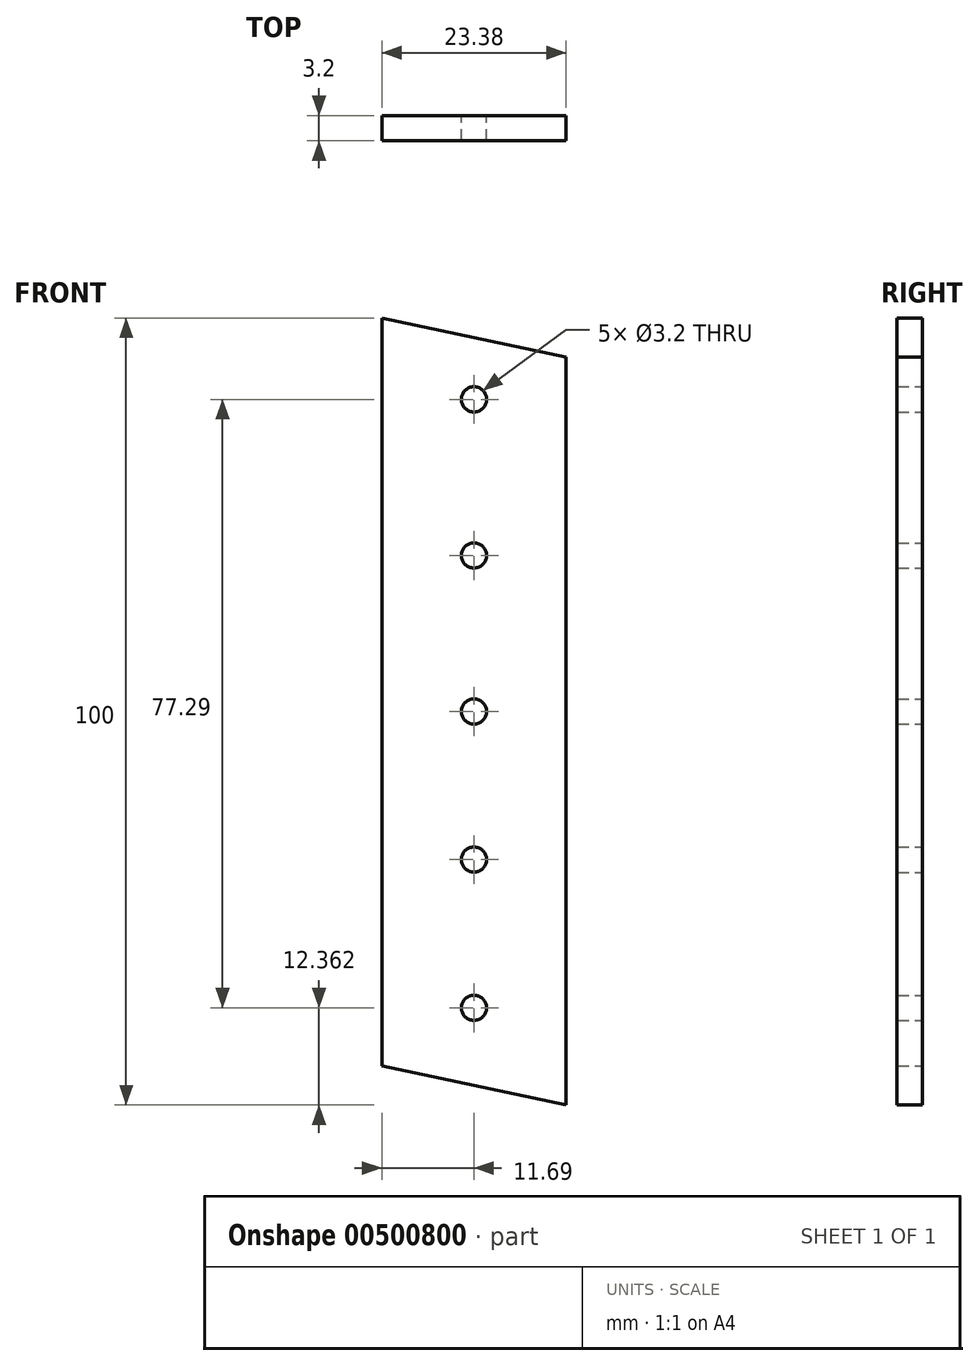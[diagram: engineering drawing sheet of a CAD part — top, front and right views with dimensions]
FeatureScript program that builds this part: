
annotation { "Feature Type Name" : "Feature", "Feature Type Description" : "" }
export const myFeature = defineFeature(function(context is Context, id is Id, definition is map)
    precondition{}
    {
        {
            var Q0;
            Q0=qCreatedBy(makeId("Front.planeOp"),FACE);
            var sketch = newSketch(context, id + "F0", { "sketchPlane" : qUnion([Q0])});
            skLineSegment(sketch, "E0.bottom", {"start": v(11.69, 45) * mm, "end": v(-11.69, 45) * mm});
            skLineSegment(sketch, "E0.top", {"start": v(11.69, -45) * mm, "end": v(-11.69, -45) * mm});
            skLineSegment(sketch, "E0.left", {"start": v(11.69, 45) * mm, "end": v(11.69, -45) * mm});
            skLineSegment(sketch, "E0.right", {"start": v(-11.69, 45) * mm, "end": v(-11.69, -45) * mm});
            skPoint(sketch, "E0.middle", {"position": v(0, 0) * mm});
            skLineSegment(sketch, "E1", {"start": v(-11.69, 45) * mm, "end": v(-11.69, 50) * mm});
            skLineSegment(sketch, "E2", {"start": v(11.69, -45) * mm, "end": v(11.69, -50) * mm});
            skLineSegment(sketch, "E3", {"start": v(-11.69, -45) * mm, "end": v(11.69, -50) * mm});
            skLineSegment(sketch, "E4", {"start": v(-11.69, 50) * mm, "end": v(11.69, 45) * mm});
            skPoint(sketch, "E5", {"position": v(0, -37.64) * mm});
            skPoint(sketch, "E6", {"position": v(0, 39.65) * mm});
            skCircle(sketch, "E7", {"center": v(0, 39.65) * mm, "radius": 1.6 * mm});
            skCircle(sketch, "E8", {"center": v(0, 0) * mm, "radius": 1.6 * mm});
            skCircle(sketch, "E9", {"center": v(0, -37.64) * mm, "radius": 1.6 * mm});
            skLineSegment(sketch, "E10", {"start": v(0, 39.65) * mm, "end": v(0, 0) * mm});
            skLineSegment(sketch, "E11", {"start": v(0, 0) * mm, "end": v(0, 19.83) * mm});
            skLineSegment(sketch, "E12", {"start": v(0, -37.64) * mm, "end": v(0, 0) * mm});
            skLineSegment(sketch, "E13", {"start": v(0, 0) * mm, "end": v(0, -18.82) * mm});
            skCircle(sketch, "E14", {"center": v(0, -18.82) * mm, "radius": 1.6 * mm});
            skCircle(sketch, "E15", {"center": v(0, 19.83) * mm, "radius": 1.6 * mm});
            skLineSegment(sketch, "E16", {"start": v(0, 0) * mm, "end": v(-11.69, 0) * mm});
            skLineSegment(sketch, "E17", {"start": v(0, -1.6) * mm, "end": v(0, 21.43) * mm});
            skLineSegment(sketch, "E18", {"start": v(-1.6, 39.64) * mm, "end": v(-1.6, 47.84) * mm});
            skLineSegment(sketch, "E19", {"start": v(1.6, 39.65) * mm, "end": v(1.6, 47.16) * mm});
            skLineSegment(sketch, "E20", {"start": v(-1.6, -37.64) * mm, "end": v(-1.6, -47.16) * mm});
            skLineSegment(sketch, "E21", {"start": v(1.6, -37.64) * mm, "end": v(1.6, -47.84) * mm});
            skSolve(sketch);
        }
        {
            var Q0;
            Q0 = qSketchRegion(id + "F0", true);
            var Q1;
            {var subQ0=sQuery(id+"F0.wireOp",EDGE,"E21");var subQ1=sQuery(id+"F0.wireOp",EDGE,"E0.top");var subQ2=makeQuery(id+"F0.imprint","INTERSECT",VERTEX,{"derivedFrom":[subQ1,subQ0]});Q1=makeQuery(id+"F0.imprint","IMPRINT",FACE,{"disambiguationData":[TD([[makeQuery(id+"F0.imprint","IMPRINT",EDGE,{"disambiguationData":[TD([[subQ2,-1.0]])],"derivedFrom":subQ1}),-1.0]])]});}
            var Q2;
            {var subQ0=sQuery(id+"F0.wireOp",EDGE,"E19");var subQ1=sQuery(id+"F0.wireOp",EDGE,"E0.bottom");var subQ2=makeQuery(id+"F0.imprint","INTERSECT",VERTEX,{"derivedFrom":[subQ1,subQ0]});Q2=makeQuery(id+"F0.imprint","IMPRINT",FACE,{"disambiguationData":[TD([[makeQuery(id+"F0.imprint","IMPRINT",EDGE,{"disambiguationData":[TD([[subQ2,-1.0]])],"derivedFrom":subQ1}),1.0]])]});}
            extrude(context, id + "F1", {"entities" : qUnion([Q0, Q1, Q2]), "depth" : 3.2 * mm, "offsetDistance" : 25 * mm});
        }
    });
